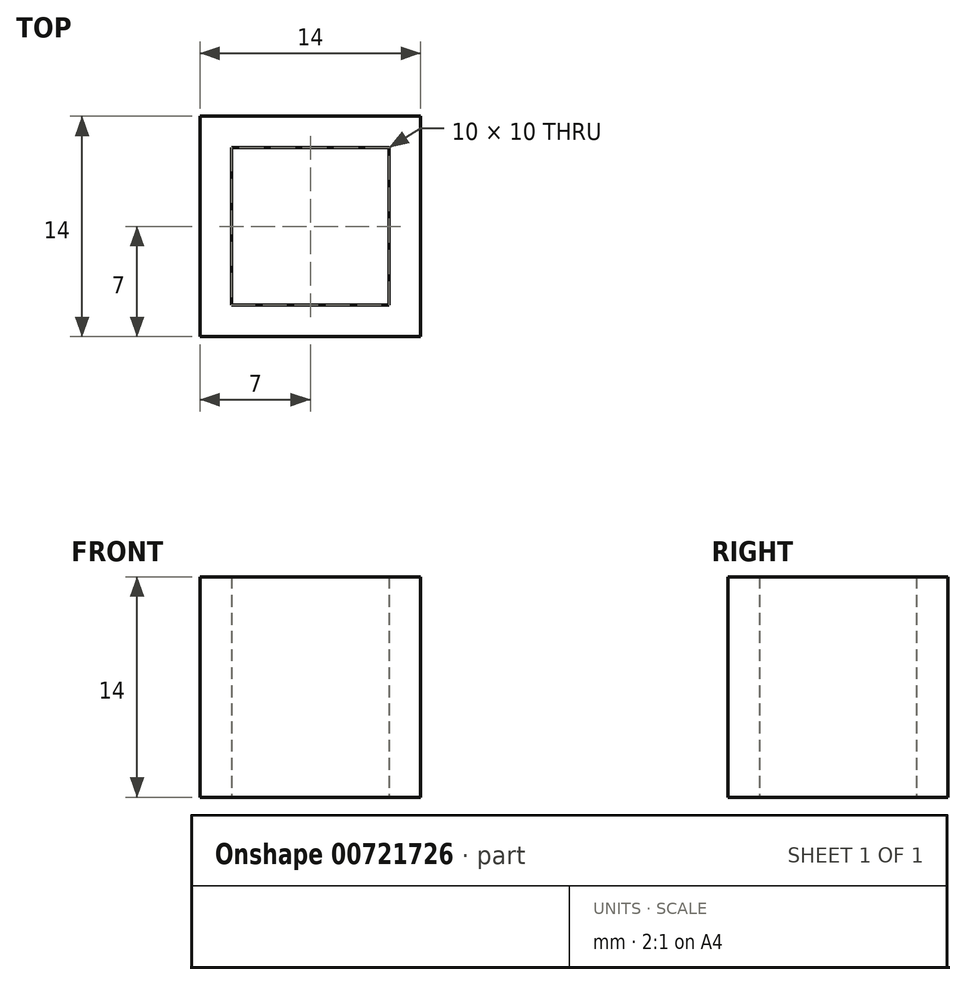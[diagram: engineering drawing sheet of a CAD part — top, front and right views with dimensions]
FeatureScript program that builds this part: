
annotation { "Feature Type Name" : "Feature", "Feature Type Description" : "" }
export const myFeature = defineFeature(function(context is Context, id is Id, definition is map)
    precondition{}
    {
        {
            var Q0;
            Q0=qCreatedBy(makeId("Top.planeOp"),FACE);
            var sketch = newSketch(context, id + "F0", { "sketchPlane" : qUnion([Q0])});
            skLineSegment(sketch, "E0.bottom", {"start": v(5, 5) * mm, "end": v(-5, 5) * mm});
            skLineSegment(sketch, "E0.top", {"start": v(5, -5) * mm, "end": v(-5, -5) * mm});
            skLineSegment(sketch, "E0.left", {"start": v(5, 5) * mm, "end": v(5, -5) * mm});
            skLineSegment(sketch, "E0.right", {"start": v(-5, 5) * mm, "end": v(-5, -5) * mm});
            skPoint(sketch, "E0.middle", {"position": v(0, 0) * mm});
            skLineSegment(sketch, "E1.bottom", {"start": v(7, 7) * mm, "end": v(-7, 7) * mm});
            skLineSegment(sketch, "E1.top", {"start": v(7, -7) * mm, "end": v(-7, -7) * mm});
            skLineSegment(sketch, "E1.left", {"start": v(7, 7) * mm, "end": v(7, -7) * mm});
            skLineSegment(sketch, "E1.right", {"start": v(-7, 7) * mm, "end": v(-7, -7) * mm});
            skSolve(sketch);
        }
        {
            var Q0;
            Q0 = qSketchRegion(id + "F0", true);
            extrude(context, id + "F1", {"entities" : qUnion([Q0]), "depth" : 14 * mm, "offsetDistance" : 25 * mm});
        }
    });
